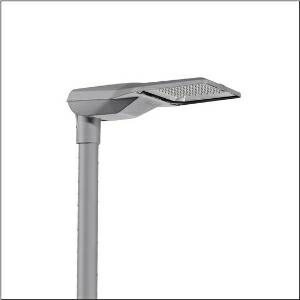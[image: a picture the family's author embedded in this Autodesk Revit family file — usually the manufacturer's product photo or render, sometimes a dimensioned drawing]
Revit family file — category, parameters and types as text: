
# Revit family: streetlight_sl_21_iq_midi___stw1_0a_5xe3e21g08nb_ca38
name_source: partatom
category: Lighting Fixtures
units: mm (PartAtom-declared; Revit-internal decimal feet)

## family parameters
Cut with Voids When Loaded = No
Host = Face
Light Source = No
Part Type = Normal
Room Calculation Point = No
Round Connector Dimension = Use Diameter
Shared = No

## types (1)
- --- (1 x LED, 19210 lm, 155.5 W, 2200K)
    Apparent Load = 155 VA
    CIE Flux Codes = 39 75 98 100 100
    Color Rendering = 70
    Color Temperature = 2200K
    Default Elevation = 1800 mm
    Description = Streetlight SL 21 iQ midi, mast luminaire, primary light control with lens, of PMMA, primary optical cover: cover, of toughened safety glass, transparent, light distribution: STW1.0a, light emission: direct distribution, primary light characteristic: asymmetric, installation type: post-top, side-entry, LED, High Power LED, rated luminous flux: 19.210lm, luminous efficacy: 124lm/W, light colour: 722, colour temperature: 2200K, control gear: iQ Street-Remote, control: Street-Remote, Auto-Match, Temp-Guard, Lumen-Switch, Night-Set, Smart-Wire, Light-Fading, Desk-Remote (wireless, voltage-free reading and setting of iQ features in the workshop via application-optimized NFC function/RFID function), optimised constant luminous flux control (CLO 2.0), pre-setting: linear dimming characteristic, mains connection: 230..240V, AC, 50/60Hz, start of lifetime: 156W, end of service life: 162W, reduction: 69W, luminaire housing, of diecast aluminium, powder-coated, SITECO metallic grey (DB 702S), corrosivity category C5 high according to DIN EN ISO 12944, please order mast flange separately, inclination adjustable: 0°, 5°, 10°, 15°, sealing non-destructively replaceable, multi-level sealing system, length: 644mm, width: 335mm, height: 110mm, mast flange for spigot size: 42mm (side-entry): 5XC10008XM4, 60/48mm (side-entry/post-top): 5XC10108XM2, 76/60mm (side-entry/post-top): 5XC10108XM1, mounting height: 4..8m, protection rating (complete): IP66, insulation class (complete): insulation class II (safety insulation), certification: CE, ENEC, ENEC+, VDE, impact resistance: IK10, permissible operating ambient temperature for outdoor applications: -40..+50°C, standard-compliant lighting for roads and squares, packaging unit: 1 piece

Light Distribution: STW1.0a
    Height = 111 mm
    Lamp = 1 x LED
    Lamp Light Flux = 19210 lm
    Lamp Power = 155.5 W
    Lamp count = 1
    Length = 644 mm
    Luminous efficacy = 124 lm/W
    Manufacturer = Siteco
    ModVariant = No
    Model = 5XE3E21G08NB
    Number of Poles = 1
    OnlyDefault = Yes
    Power Factor = 1
    Product Name = Streetlight SL 21 iQ midi | STW1.0a
    Product group = mast luminaire | pylon top
    ProductGroupID = 6100
    Protection Class = Protection class II
    Protection Degree = IP 66
    RLX_Detail_Level = 1
    RLX_Emergency_Light_Flux = 0 lm
    RLX_Emergency_Type = 0
    RLX_Emergency_Type_DB = No
    RlxData = <blob elided: 27285 chars, md5=6da595a3>
    Socket = socket
    Standby Power = 0 W
    System Light Flux = 19210 lm
    System Power = 155 W
    Type Comments = factory setting: luminous flux: 100 % | dim-lin: 254 | 823 mA
    Type Image = l_1004298.jpg
    URL = http://relux.com
    VarID = @adj_169441
    Voltage = 0 V
    Weight = 0.00 kg
    Width = 336 mm

## geometry (parser evidence)
native form markers: Blend x4, Sweep x12
no freeform markers — native parametric forms only
